# Revit family: Haworth_Epure_Benches_withColumnLegs_DoubleEndModule_EU_PRELIMINARY
name_source: partatom
category: Furniture
units: mm (PartAtom-declared; Revit-internal decimal feet)

## family parameters
Always vertical = Yes
Cut with Voids When Loaded = No
OmniClass Number = 23.40.70.14.64.11
OmniClass Title = Office Furniture
Room Calculation Point = No
Shared = No
Work Plane-Based = No

## types (6) — shared parameters
Actual Height = 73 cm
Assembly Code = E2020200
Description = Haworth - Epure - Benches - Bench with Column Leg - Double End Module
Flip Top Finish = Haworth _ Paint _ Metallic Silver
Leg Height = 70 cm
Manufacturer = Haworth
Model = EUB3CXXXX
Revision Number = 1
Size = Verify Final Dim.w/ Haworth
Trim Finish = Haworth _ Metal _ Structured White EC
URL = https://www.haworth.com
URL - Product = https://www.haworth.com
Warranty = http://www.haworth.com
Worksurface Depth = 160, 180, 200 cm
Worksurface Width = 120, 140, 160, 180, 200 cm

## per-type parameters (varying)
| type | Accessory Kit | Actual Depth | Actual Width | Cable Tray Double | Cable Tray Single | Cable Tray Width | Central Rail | Depth | Flip Top Cable Outlet | No Accessory Kit | Rectangle | Round Cable Outlet | Scallop | Void Depth |
| 120 x 160 | No | 160 cm | 120 cm | No | No | 60 cm | No | 80 cm | No | Yes | Yes | No | No | 0 cm |
| 200 x 160 | Yes | 160 cm | 200 cm | No | No | 140 cm | No | 80 cm | No | No | No | Yes | Yes | 3 cm |
| 140 x 180 | Yes | 180 cm | 140 cm | Yes | No | 80 cm | No | 90 cm | No | No | No | No | Yes | 3 cm |
| 180 x 180 | Yes | 180 cm | 180 cm | No | No | 120 cm | No | 90 cm | Yes | No | Yes | No | No | 0 cm |
| 160 x 200 | Yes | 200 cm | 160 cm | No | Yes | 100 cm | Yes | 99 cm | No | No | Yes | No | No | 0 cm |
| 200 x 200 | No | 200 cm | 200 cm | No | No | 140 cm | Yes | 99 cm | No | Yes | Yes | No | No | 0 cm |

## geometry (parser evidence)
native form markers: Blend x8, Sweep x30
no freeform markers — native parametric forms only
